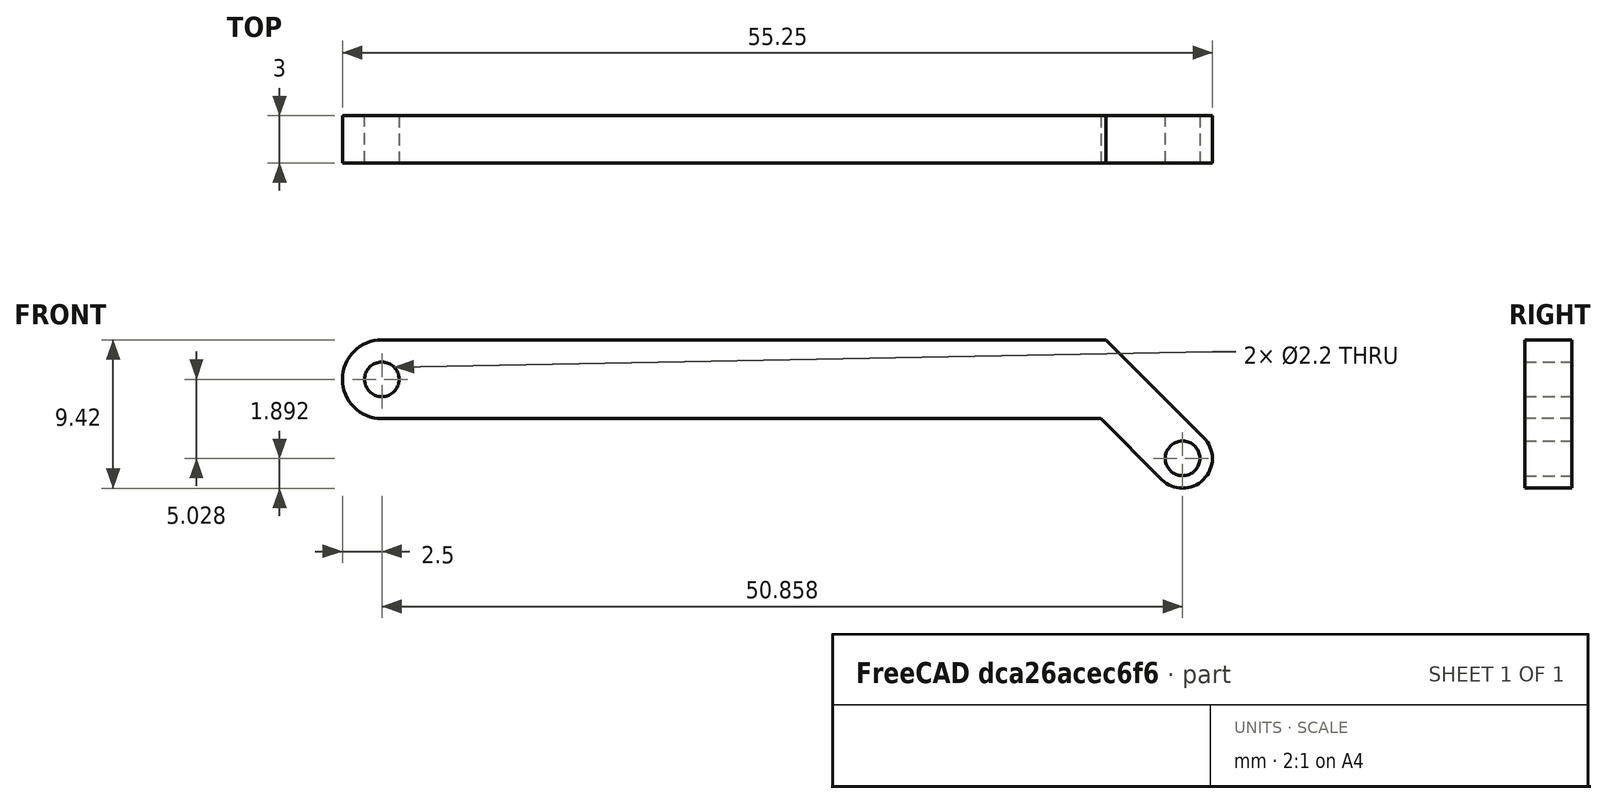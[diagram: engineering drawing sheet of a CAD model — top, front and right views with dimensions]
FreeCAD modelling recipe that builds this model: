
FCSTD DOCUMENT  (FreeCAD 0.20R29603 (Git))
Label: ServoLinkage
License: All rights reserved
LicenseURL: http://en.wikipedia.org/wiki/All_rights_reserved
objects: Sketcher::SketchObject×1, PartDesign::Pad×1, PartDesign::CoordinateSystem×1, PartDesign::Body×1
note: 5 computed .brp shape members not serialized (recipe doc carries the construction recipe); baked Part::Feature solids carry a one-line shape summary decoded from their .brp

FEATURE [Sketcher::SketchObject] Sketch
  FullyConstrained = false
  MapMode = 5
  Placement = pos=(0,0,0) rot=(1,0,0;1.5708rad)
  Support = -> [XZ_Plane]
  sketch-geometry (9):
    g0: Circle CenterX=0 CenterY=0 CenterZ=0 NormalX=0 NormalY=0 NormalZ=1 AngleXU=0 Radius=1.1
    g1: ArcOfCircle CenterX=0 CenterY=0 CenterZ=0 NormalX=0 NormalY=0 NormalZ=1 AngleXU=0 Radius=2.5 StartAngle=1.5708 EndAngle=4.71239
    g2: LineSegment StartX=-4e-16 StartY=2.5 StartZ=0 EndX=46 EndY=2.5 EndZ=0
    g3: LineSegment StartX=-5e-16 StartY=-2.5 StartZ=0 EndX=45.6612 EndY=-2.5 EndZ=0
    g4: LineSegment StartX=45.6612 StartY=-2.5 StartZ=0 EndX=49.5238 EndY=-6.36264 EndZ=0
    g5: LineSegment StartX=46 StartY=2.5 StartZ=0 EndX=52.1932 EndY=-3.69323 EndZ=0
    g6: Circle CenterX=50.8585 CenterY=-5.02793 CenterZ=0 NormalX=0 NormalY=0 NormalZ=1 AngleXU=0 Radius=1.1
    g7: ArcOfCircle CenterX=50.8585 CenterY=-5.02793 CenterZ=0 NormalX=0 NormalY=0 NormalZ=1 AngleXU=0 Radius=1.88756 StartAngle=3.92699 EndAngle=7.06858
    g8: LineSegment StartX=49.5238 StartY=-6.36264 StartZ=0 EndX=52.1932 EndY=-3.69323 EndZ=0
  constraints (19):
    c: Coincident(g0,g-1)
    c: Coincident(g1,g0)
    c: Diameter(g0) = 2.2
    c: Tangent(g1,g2) = 1.5708
    c: Tangent(g3,g1) = -1.5708
    c: Parallel(g2,g3)
    c: Diameter(g1) = 5
    c: Horizontal(g2)
    c: Coincident(g4,g3)
    c: Coincident(g5,g2)
    c: Parallel(g5,g4)
    c: Equal(g0,g6)
    c: Tangent(g7,g5) = 1.5708
    c: Tangent(g7,g4) = -1.5708
    c: Coincident(g8,g4)
    c: Coincident(g8,g5)
    c: Coincident(g6,g7)
    c: Angle(g5) = -0.785398
    c: DistanceX(g2,g2) = 46
FEATURE [PartDesign::Pad] Pad
  Direction = (0,-1,2e-16)
  Length = 3
  Length2 = 10
  Placement = pos=(0,0,0) rot=(1,0,0;1.5708rad)
  Profile = -> Sketch
  ReferenceAxis = -> Sketch [N_Axis]
  Type = 0
FEATURE [PartDesign::CoordinateSystem] LCS_1
  AttacherType = Attacher::AttachEngine3D
  MapMode = 11
  Placement = pos=(0,-3,7e-16) rot=(0.57735,-0.57735,0.57735;2.0944rad)
  Support = -> [Pad]
FEATURE [PartDesign::Body] Body
  Group = -> [Sketch,Pad,LCS_1]
  Origin = -> Origin
  Tip = -> Pad
